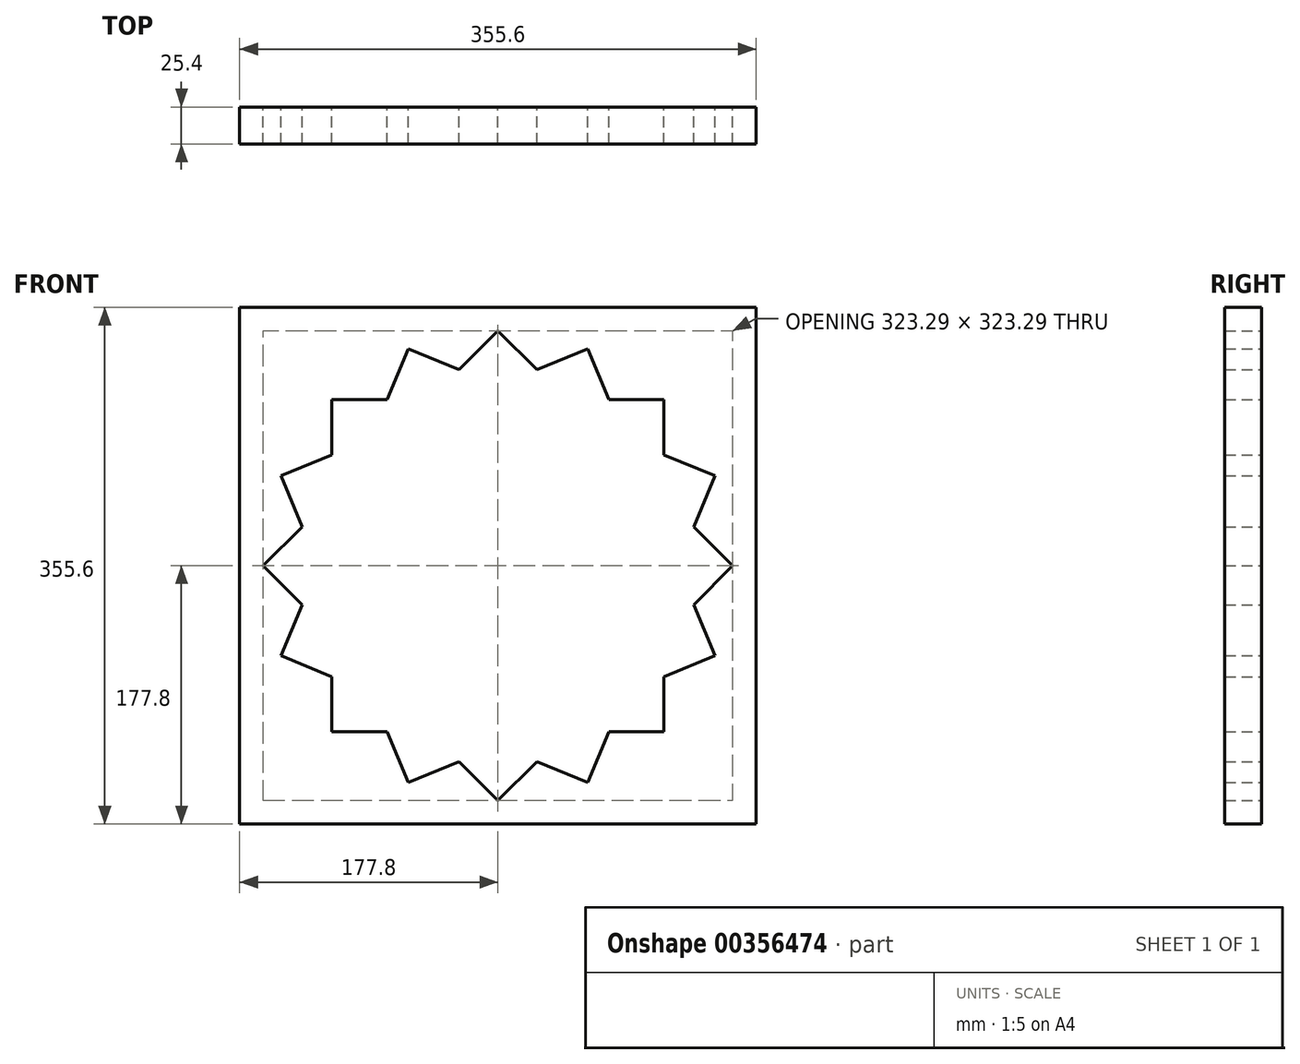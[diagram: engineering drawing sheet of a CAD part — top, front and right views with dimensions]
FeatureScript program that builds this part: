
annotation { "Feature Type Name" : "Feature", "Feature Type Description" : "" }
export const myFeature = defineFeature(function(context is Context, id is Id, definition is map)
    precondition{}
    {
        {
            var Q0;
            Q0=qCreatedBy(makeId("Front.planeOp"),FACE);
            var sketch = newSketch(context, id + "F0", { "sketchPlane" : qUnion([Q0])});
            skLineSegment(sketch, "E0.bottom", {"start": v(177.8, 177.8) * mm, "end": v(-177.8, 177.8) * mm});
            skLineSegment(sketch, "E0.top", {"start": v(177.8, -177.8) * mm, "end": v(-177.8, -177.8) * mm});
            skLineSegment(sketch, "E0.left", {"start": v(177.8, 177.8) * mm, "end": v(177.8, -177.8) * mm});
            skLineSegment(sketch, "E0.right", {"start": v(-177.8, 177.8) * mm, "end": v(-177.8, -177.8) * mm});
            skPoint(sketch, "E0.middle", {"position": v(0, 0) * mm});
            skLineSegment(sketch, "E1.bottom", {"start": v(114.3, 114.3) * mm, "end": v(-114.3, 114.3) * mm});
            skLineSegment(sketch, "E1.top", {"start": v(114.3, -114.3) * mm, "end": v(-114.3, -114.3) * mm});
            skLineSegment(sketch, "E1.left", {"start": v(114.3, 114.3) * mm, "end": v(114.3, -114.3) * mm});
            skLineSegment(sketch, "E1.right", {"start": v(-114.3, 114.3) * mm, "end": v(-114.3, -114.3) * mm});
            skLineSegment(sketch, "E2.1.0", {"start": v(149.34, 61.86) * mm, "end": v(-61.86, 149.34) * mm});
            skLineSegment(sketch, "E2.1.1", {"start": v(149.34, 61.86) * mm, "end": v(61.86, -149.34) * mm});
            skLineSegment(sketch, "E2.1.2", {"start": v(61.86, -149.34) * mm, "end": v(-149.34, -61.86) * mm});
            skLineSegment(sketch, "E2.1.3", {"start": v(-61.86, 149.34) * mm, "end": v(-149.34, -61.86) * mm});
            skLineSegment(sketch, "E2.2.0", {"start": v(161.64, 0) * mm, "end": v(0, 161.64) * mm});
            skLineSegment(sketch, "E2.2.1", {"start": v(161.64, 0) * mm, "end": v(0, -161.64) * mm});
            skLineSegment(sketch, "E2.2.2", {"start": v(0, -161.64) * mm, "end": v(-161.64, 0) * mm});
            skLineSegment(sketch, "E2.2.3", {"start": v(0, 161.64) * mm, "end": v(-161.64, 0) * mm});
            skLineSegment(sketch, "E2.anchor1", {"start": v(0, 0) * mm, "end": v(-114.3, 114.3) * mm, "construction": true});
            skLineSegment(sketch, "E2.anchor2", {"start": v(0, 0) * mm, "end": v(114.3, -114.3) * mm, "construction": true});
            skLineSegment(sketch, "E3.2.3.0", {"start": v(149.34, -61.86) * mm, "end": v(61.86, 149.34) * mm});
            skLineSegment(sketch, "E3.3.3.0", {"start": v(149.34, -61.86) * mm, "end": v(-61.86, -149.34) * mm});
            skLineSegment(sketch, "E3.6.3.0", {"start": v(-61.86, -149.34) * mm, "end": v(-149.34, 61.86) * mm});
            skLineSegment(sketch, "E3.9.3.0", {"start": v(61.86, 149.34) * mm, "end": v(-149.34, 61.86) * mm});
            skLineSegment(sketch, "E3.2.4.0", {"start": v(114.3, -114.3) * mm, "end": v(114.3, 114.3) * mm});
            skLineSegment(sketch, "E3.6.4.0", {"start": v(-114.3, -114.3) * mm, "end": v(-114.3, 114.3) * mm});
            skLineSegment(sketch, "E3.2.5.0", {"start": v(61.86, -149.34) * mm, "end": v(149.34, 61.86) * mm});
            skLineSegment(sketch, "E3.6.5.0", {"start": v(-149.34, -61.86) * mm, "end": v(-61.86, 149.34) * mm});
            skLineSegment(sketch, "E3.2.6.0", {"start": v(0, -161.64) * mm, "end": v(161.64, 0) * mm});
            skLineSegment(sketch, "E3.6.6.0", {"start": v(-161.64, 0) * mm, "end": v(0, 161.64) * mm});
            skLineSegment(sketch, "E3.2.7.0", {"start": v(-61.86, -149.34) * mm, "end": v(149.34, -61.86) * mm});
            skLineSegment(sketch, "E3.3.7.0", {"start": v(-61.86, -149.34) * mm, "end": v(-149.34, 61.86) * mm});
            skLineSegment(sketch, "E3.6.7.0", {"start": v(-149.34, 61.86) * mm, "end": v(61.86, 149.34) * mm});
            skLineSegment(sketch, "E3.9.7.0", {"start": v(149.34, -61.86) * mm, "end": v(61.86, 149.34) * mm});
            skLineSegment(sketch, "E3.2.8.0", {"start": v(-114.3, -114.3) * mm, "end": v(114.3, -114.3) * mm});
            skLineSegment(sketch, "E3.3.8.0", {"start": v(-114.3, -114.3) * mm, "end": v(-114.3, 114.3) * mm});
            skLineSegment(sketch, "E3.6.8.0", {"start": v(-114.3, 114.3) * mm, "end": v(114.3, 114.3) * mm});
            skLineSegment(sketch, "E3.9.8.0", {"start": v(114.3, -114.3) * mm, "end": v(114.3, 114.3) * mm});
            skSolve(sketch);
        }
        {
            var Q0;
            Q0 = qSketchRegion(id + "F0", true);
            extrude(context, id + "F1", {"entities" : qUnion([Q0]), "depth" : 25.4 * mm});
        }
    });
